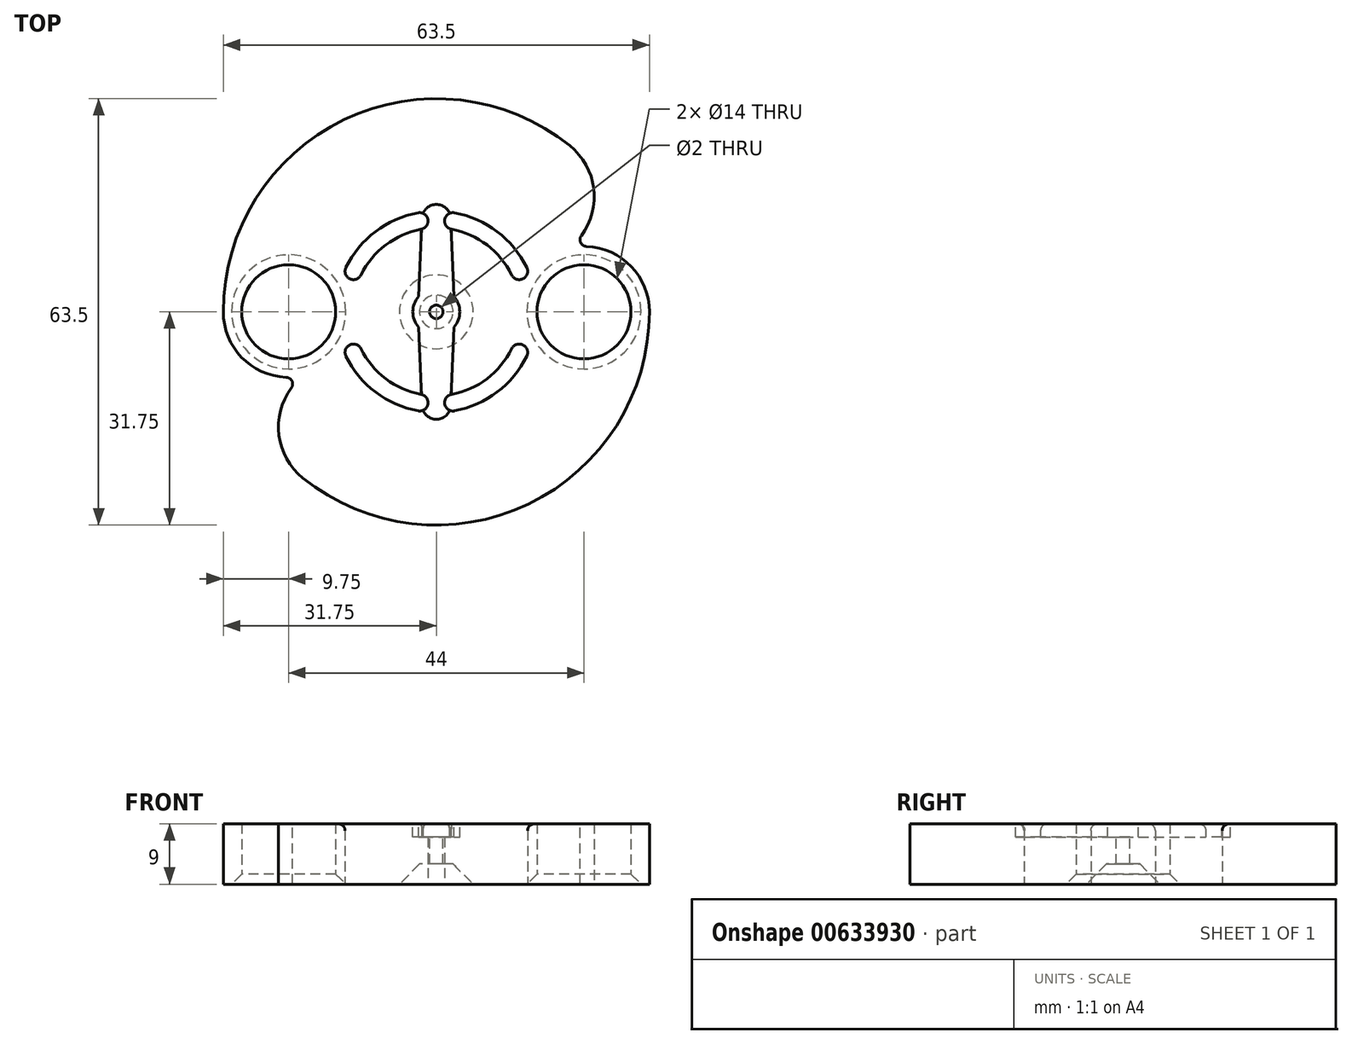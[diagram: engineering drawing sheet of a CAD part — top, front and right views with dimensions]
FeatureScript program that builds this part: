
annotation { "Feature Type Name" : "Feature", "Feature Type Description" : "" }
export const myFeature = defineFeature(function(context is Context, id is Id, definition is map)
    precondition{}
    {
        {
            var Q0;
            Q0=qCreatedBy(makeId("Top.planeOp"),FACE);
            var sketch = newSketch(context, id + "F0", { "sketchPlane" : qUnion([Q0])});
            skCircle(sketch, "E0", {"center": v(0, 0) * mm, "radius": 32.5 * mm});
            skCircle(sketch, "E1", {"center": v(0, 0) * mm, "radius": 2.5 * mm});
            skCircle(sketch, "E2", {"center": v(22, 0) * mm, "radius": 7 * mm});
            skLineSegment(sketch, "E3", {"start": v(0, 0) * mm, "end": v(22, 0) * mm, "construction": true});
            skLineSegment(sketch, "E4", {"start": v(0, 0) * mm, "end": v(-22, 0) * mm, "construction": true});
            skCircle(sketch, "E5", {"center": v(-22, 0) * mm, "radius": 7 * mm});
            skSolve(sketch);
        }
        {
            var Q0;
            Q0=qSketchRegion(id+"F0",true);
            extrude(context, id + "F1", {"entities" : qUnion([Q0]), "endBound" : BoundingType.SYMMETRIC, "depth" : 9 * mm, "offsetDistance" : 25 * mm});
        }
        {
            var Q0;
            Q0=makeQuery(id+"F1.opExtrude","CAP_FACE",FACE,{"disambiguationData":[OSD([sQuery(id+"F0.wireOp",EDGE,"E0"),sQuery(id+"F0.wireOp",EDGE,"E1"),sQuery(id+"F0.wireOp",EDGE,"E2")])],"isStart":false});
            var sketch = newSketch(context, id + "F2", { "sketchPlane" : qUnion([Q0])});
            skCircle(sketch, "E6", {"center": v(0, 0) * mm, "radius": 1 * mm});
            skCircle(sketch, "E7", {"center": v(0, 0) * mm, "radius": 2.5 * mm});
            skSolve(sketch);
        }
        {
            var Q0;
            Q0=qSketchRegion(id+"F2",true);
            extrude(context, id + "F3", {"entities" : qUnion([Q0]), "operationType" : NewBodyOperationType.ADD, "oppositeDirection" : true, "depth" : 6 * mm, "offsetDistance" : 25 * mm});
        }
        {
            var Q0;
            Q0=makeQuery(id+"F1.opExtrude","CAP_FACE",FACE,{"disambiguationData":[OSD([sQuery(id+"F0.wireOp",EDGE,"E0"),sQuery(id+"F0.wireOp",EDGE,"E1"),sQuery(id+"F0.wireOp",EDGE,"E2")])],"isStart":true});
            var sketch = newSketch(context, id + "F4", { "sketchPlane" : qUnion([Q0])});
            skLineSegment(sketch, "E8", {"start": v(0, 0) * mm, "end": v(22, 0) * mm, "construction": true});
            skCircle(sketch, "E9", {"center": v(0, 0) * mm, "radius": 32.5 * mm});
            skArc(sketch, "E10", {"start": v(12.25, 0) * mm, "mid": v(5.3, 11.05) * mm, "end": v(-7.67, 9.55) * mm});
            skArc(sketch, "E11", {"start": v(31.75, 0) * mm, "mid": v(13.72, 28.63) * mm, "end": v(-19.9, 24.75) * mm});
            skLineSegment(sketch, "E12", {"start": v(0, 0) * mm, "end": v(-22, 0) * mm, "construction": true});
            skArc(sketch, "E13", {"start": v(-12.25, 0) * mm, "mid": v(-22, 9.75) * mm, "end": v(-31.75, 0) * mm});
            skArc(sketch, "E14", {"start": v(12.25, 0) * mm, "mid": v(22, -9.75) * mm, "end": v(31.75, 0) * mm});
            skCircle(sketch, "E15", {"center": v(0, 0) * mm, "radius": 22 * mm, "construction": true});
            skArc(sketch, "E16", {"start": v(-15.94, 7.64) * mm, "mid": v(-11.6, 7.65) * mm, "end": v(-7.67, 9.55) * mm});
            skArc(sketch, "E17.trimOffspring", {"start": v(-19.9, 24.75) * mm, "mid": v(-23.53, 17.12) * mm, "end": v(-19.84, 9.5) * mm});
            skArc(sketch, "E18", {"start": v(15.94, -7.64) * mm, "mid": v(11.6, -7.65) * mm, "end": v(7.67, -9.55) * mm});
            skArc(sketch, "E19.trimOffspring", {"start": v(19.9, -24.75) * mm, "mid": v(23.53, -17.12) * mm, "end": v(19.84, -9.5) * mm});
            skArc(sketch, "E20.trimOffspring", {"start": v(-12.25, 0) * mm, "mid": v(-5.3, -11.05) * mm, "end": v(7.67, -9.55) * mm});
            skArc(sketch, "E21.trimOffspring", {"start": v(-31.75, 0) * mm, "mid": v(-13.72, -28.63) * mm, "end": v(19.9, -24.75) * mm});
            skSolve(sketch);
        }
        {
            var Q0;
            Q0=qSketchRegion(id+"F4",true);
            extrude(context, id + "F5", {"entities" : qUnion([Q0]), "operationType" : NewBodyOperationType.REMOVE, "oppositeDirection" : true, "depth" : 5 * mm, "offsetDistance" : 25 * mm});
        }
        {
            var Q0;
            Q0=makeQuery(id+"F3.boolean.opBoolean","MERGE",FACE,{"derivedFrom":[makeQuery(id+"F1.opExtrude","CAP_FACE",FACE,{"disambiguationData":[OSD([sQuery(id+"F0.wireOp",EDGE,"E0"),sQuery(id+"F0.wireOp",EDGE,"E1"),sQuery(id+"F0.wireOp",EDGE,"E2")])],"isStart":false}),makeQuery(id+"F3.opExtrude","CAP_FACE",FACE,{"disambiguationData":[OSD([sQuery(id+"F2.wireOp",EDGE,"E6"),sQuery(id+"F2.wireOp",EDGE,"E7")])],"isStart":true})]});
            var sketch = newSketch(context, id + "F6", { "sketchPlane" : qUnion([Q0])});
            skCircle(sketch, "E22", {"center": v(0, 0) * mm, "radius": 3.5 * mm});
            skLineSegment(sketch, "E23", {"start": v(0, 0) * mm, "end": v(0, 16) * mm, "construction": true});
            skLineSegment(sketch, "E24", {"start": v(0, 0) * mm, "end": v(0, -16) * mm, "construction": true});
            skArc(sketch, "E25", {"start": v(2.15, 13.85) * mm, "mid": v(0, 16) * mm, "end": v(-2.15, 13.85) * mm});
            skArc(sketch, "E26", {"start": v(-2.15, -13.85) * mm, "mid": v(0, -16) * mm, "end": v(2.15, -13.85) * mm});
            skLineSegment(sketch, "E27", {"start": v(-2.65, -2.29) * mm, "end": v(2.65, -2.29) * mm, "construction": true});
            skLineSegment(sketch, "E28", {"start": v(2.65, 2.29) * mm, "end": v(-2.65, 2.29) * mm, "construction": true});
            skLineSegment(sketch, "E29", {"start": v(2.65, -2.29) * mm, "end": v(2.15, -13.85) * mm});
            skLineSegment(sketch, "E30", {"start": v(-2.15, -13.85) * mm, "end": v(-2.65, -2.29) * mm});
            skLineSegment(sketch, "E31", {"start": v(-2.65, 2.29) * mm, "end": v(-2.15, 13.85) * mm});
            skLineSegment(sketch, "E32", {"start": v(2.65, 2.29) * mm, "end": v(2.15, 13.85) * mm});
            skSolve(sketch);
        }
        {
            var Q0;
            Q0=qSketchRegion(id+"F6",true);
            extrude(context, id + "F7", {"entities" : qUnion([Q0]), "operationType" : NewBodyOperationType.REMOVE, "oppositeDirection" : true, "depth" : 2 * mm, "offsetDistance" : 25 * mm});
        }
        {
            var Q0;
            Q0=qSketchRegion(id+"F6",true);
            extrude(context, id + "F8", {"entities" : qUnion([Q0]), "operationType" : NewBodyOperationType.REMOVE, "oppositeDirection" : true, "depth" : 2 * mm, "offsetDistance" : 25 * mm});
        }
        {
            var Q0;
            Q0=makeQuery(id+"F5.boolean.opBoolean","COPY",FACE,{"derivedFrom":makeQuery(id+"F5.opExtrude","CAP_FACE",FACE,{"disambiguationData":[OSD([sQuery(id+"F4.wireOp",EDGE,"E9"),sQuery(id+"F4.wireOp",EDGE,"E11"),sQuery(id+"F4.wireOp",EDGE,"E13"),sQuery(id+"F4.wireOp",EDGE,"E14"),sQuery(id+"F4.wireOp",EDGE,"E17.trimOffspring"),sQuery(id+"F4.wireOp",EDGE,"E19.trimOffspring"),sQuery(id+"F4.wireOp",EDGE,"E21.trimOffspring")])],"isStart":false})});
            var sketch = newSketch(context, id + "F9", { "sketchPlane" : qUnion([Q0])});
            skArc(sketch, "E33", {"start": v(19.84, -9.5) * mm, "mid": v(28.08, -7.62) * mm, "end": v(31.75, 0) * mm});
            skArc(sketch, "E34", {"start": v(-19.84, 9.5) * mm, "mid": v(-28.08, 7.62) * mm, "end": v(-31.75, 0) * mm});
            skArc(sketch, "E35", {"start": v(-19.9, 24.75) * mm, "mid": v(-23.53, 17.12) * mm, "end": v(-19.84, 9.5) * mm});
            skArc(sketch, "E36", {"start": v(31.75, 0) * mm, "mid": v(13.72, 28.63) * mm, "end": v(-19.9, 24.75) * mm});
            skCircle(sketch, "E37", {"center": v(0, 0) * mm, "radius": 32.5 * mm});
            skArc(sketch, "E38.trimOffspring", {"start": v(-31.75, 0) * mm, "mid": v(-13.72, -28.63) * mm, "end": v(19.9, -24.75) * mm});
            skArc(sketch, "E39", {"start": v(19.9, -24.75) * mm, "mid": v(23.53, -17.12) * mm, "end": v(19.84, -9.5) * mm});
            skSolve(sketch);
        }
        {
            var Q0;
            Q0=qSketchRegion(id+"F9",true);
            extrude(context, id + "F10", {"entities" : qUnion([Q0]), "operationType" : NewBodyOperationType.REMOVE, "endBound" : BoundingType.THROUGH_ALL, "oppositeDirection" : true, "depth" : 25 * mm, "offsetDistance" : 25 * mm});
        }
        {
            var Q0;
            Q0=makeQuery(id+"F1.opExtrude","CAP_FACE",FACE,{"disambiguationData":[OSD([sQuery(id+"F0.wireOp",EDGE,"E0"),sQuery(id+"F0.wireOp",EDGE,"E1"),sQuery(id+"F0.wireOp",EDGE,"E2"),sQuery(id+"F0.wireOp",EDGE,"E5")])],"isStart":true});
            var sketch = newSketch(context, id + "F11", { "sketchPlane" : qUnion([Q0])});
            skArc(sketch, "E40", {"start": v(2.71, -14.75) * mm, "mid": v(9.07, -11.95) * mm, "end": v(13.48, -6.59) * mm});
            skArc(sketch, "E41", {"start": v(2.26, -12.3) * mm, "mid": v(7.55, -9.96) * mm, "end": v(11.23, -5.49) * mm});
            skArc(sketch, "E42", {"start": v(11.23, 5.49) * mm, "mid": v(12.9, 4.92) * mm, "end": v(13.48, 6.59) * mm});
            skArc(sketch, "E43", {"start": v(13.48, -6.59) * mm, "mid": v(12.9, -4.92) * mm, "end": v(11.23, -5.49) * mm});
            skArc(sketch, "E44", {"start": v(-2.71, -14.75) * mm, "mid": v(-1.26, -13.75) * mm, "end": v(-2.26, -12.3) * mm});
            skArc(sketch, "E45", {"start": v(2.26, -12.3) * mm, "mid": v(1.26, -13.75) * mm, "end": v(2.71, -14.75) * mm});
            skArc(sketch, "E46", {"start": v(-2.26, 12.3) * mm, "mid": v(-1.26, 13.75) * mm, "end": v(-2.71, 14.75) * mm});
            skArc(sketch, "E47", {"start": v(2.71, 14.75) * mm, "mid": v(1.26, 13.75) * mm, "end": v(2.26, 12.3) * mm});
            skArc(sketch, "E48.trimOffspring", {"start": v(11.23, 5.49) * mm, "mid": v(7.55, 9.96) * mm, "end": v(2.26, 12.3) * mm});
            skArc(sketch, "E49.trimOffspring", {"start": v(13.48, 6.59) * mm, "mid": v(9.07, 11.95) * mm, "end": v(2.71, 14.75) * mm});
            skArc(sketch, "E50.trimOffspring", {"start": v(-2.26, 12.3) * mm, "mid": v(-7.55, 9.96) * mm, "end": v(-11.23, 5.5) * mm});
            skArc(sketch, "E51.trimOffspring", {"start": v(-2.71, 14.75) * mm, "mid": v(-9.06, 11.95) * mm, "end": v(-13.47, 6.6) * mm});
            skArc(sketch, "E52.trimOffspring", {"start": v(-13.48, -6.59) * mm, "mid": v(-9.07, -11.95) * mm, "end": v(-2.71, -14.75) * mm});
            skArc(sketch, "E53.trimOffspring", {"start": v(-11.23, -5.49) * mm, "mid": v(-7.55, -9.96) * mm, "end": v(-2.26, -12.3) * mm});
            skArc(sketch, "E54", {"start": v(-11.23, -5.49) * mm, "mid": v(-12.9, -4.92) * mm, "end": v(-13.48, -6.59) * mm});
            skArc(sketch, "E55", {"start": v(-13.47, 6.6) * mm, "mid": v(-12.9, 4.92) * mm, "end": v(-11.23, 5.5) * mm});
            skSolve(sketch);
        }
        {
            var Q0;
            Q0=qSketchRegion(id+"F11",true);
            extrude(context, id + "F12", {"entities" : qUnion([Q0]), "operationType" : NewBodyOperationType.REMOVE, "endBound" : BoundingType.THROUGH_ALL, "oppositeDirection" : true, "depth" : 25 * mm, "offsetDistance" : 25 * mm});
        }
        {
            var Q0;
            Q0=makeQuery(id+"F1.opExtrude","CAP_EDGE",EDGE,{"disambiguationData":[OSD([sQuery(id+"F0.wireOp",EDGE,"E2")])],"isStart":true});
            var Q1;
            Q1=makeQuery(id+"F1.opExtrude","CAP_EDGE",EDGE,{"disambiguationData":[OSD([sQuery(id+"F0.wireOp",EDGE,"E5")])],"isStart":true});
            chamfer(context, id + "F13", {"entities" : qUnion([Q0, Q1]), "width" : 1.5 * mm, "tangentPropagation" : true});
        }
        {
            var Q0;
            Q0=makeQuery(id+"F10.boolean.opBoolean","MERGE",EDGE,{"derivedFrom":[makeQuery(id+"F5.boolean.opBoolean","COPY",EDGE,{"derivedFrom":makeQuery(id+"F5.opExtrude","SWEPT_EDGE",EDGE,{"disambiguationData":[OSD([sQuery(id+"F4.wireOp",EDGE,"E13"),sQuery(id+"F4.wireOp",EDGE,"E17.trimOffspring")])]})}),makeQuery(id+"F10.opExtrude","SWEPT_EDGE",EDGE,{"disambiguationData":[OSD([sQuery(id+"F9.wireOp",EDGE,"E34"),sQuery(id+"F9.wireOp",EDGE,"E35")])]})]});
            var Q1;
            Q1=makeQuery(id+"F10.boolean.opBoolean","MERGE",EDGE,{"derivedFrom":[makeQuery(id+"F5.boolean.opBoolean","COPY",EDGE,{"derivedFrom":makeQuery(id+"F5.opExtrude","SWEPT_EDGE",EDGE,{"disambiguationData":[OSD([sQuery(id+"F4.wireOp",EDGE,"E14"),sQuery(id+"F4.wireOp",EDGE,"E19.trimOffspring")])]})}),makeQuery(id+"F10.opExtrude","SWEPT_EDGE",EDGE,{"disambiguationData":[OSD([sQuery(id+"F9.wireOp",EDGE,"E33"),sQuery(id+"F9.wireOp",EDGE,"E39")])]})]});
            fillet(context, id + "F14", {"entities" : qUnion([Q0, Q1]), "radius" : 1 * mm, "tangentPropagation" : true, "allowEdgeOverflow" : false});
        }
        {
            var Q0;
            Q0=makeQuery(id+"F12.boolean.opBoolean","INTERSECT",EDGE,{"derivedFrom":[makeQuery(id+"F3.boolean.opBoolean","MERGE",FACE,{"derivedFrom":[makeQuery(id+"F1.opExtrude","CAP_FACE",FACE,{"disambiguationData":[OSD([sQuery(id+"F0.wireOp",EDGE,"E0"),sQuery(id+"F0.wireOp",EDGE,"E1"),sQuery(id+"F0.wireOp",EDGE,"E2"),sQuery(id+"F0.wireOp",EDGE,"E5")])],"isStart":false}),makeQuery(id+"F3.opExtrude","CAP_FACE",FACE,{"disambiguationData":[OSD([sQuery(id+"F2.wireOp",EDGE,"E6"),sQuery(id+"F2.wireOp",EDGE,"E7")])],"isStart":true})]}),makeQuery(id+"F12.opExtrude","SWEPT_FACE",FACE,{"disambiguationData":[OSD([sQuery(id+"F11.wireOp",EDGE,"E52.trimOffspring")])]})]});
            var Q1;
            Q1=makeQuery(id+"F12.boolean.opBoolean","INTERSECT",EDGE,{"derivedFrom":[makeQuery(id+"F3.boolean.opBoolean","MERGE",FACE,{"derivedFrom":[makeQuery(id+"F1.opExtrude","CAP_FACE",FACE,{"disambiguationData":[OSD([sQuery(id+"F0.wireOp",EDGE,"E0"),sQuery(id+"F0.wireOp",EDGE,"E1"),sQuery(id+"F0.wireOp",EDGE,"E2"),sQuery(id+"F0.wireOp",EDGE,"E5")])],"isStart":false}),makeQuery(id+"F3.opExtrude","CAP_FACE",FACE,{"disambiguationData":[OSD([sQuery(id+"F2.wireOp",EDGE,"E6"),sQuery(id+"F2.wireOp",EDGE,"E7")])],"isStart":true})]}),makeQuery(id+"F12.opExtrude","SWEPT_FACE",FACE,{"disambiguationData":[OSD([sQuery(id+"F11.wireOp",EDGE,"E51.trimOffspring")])]})]});
            var Q2;
            Q2=makeQuery(id+"F12.boolean.opBoolean","COPY",EDGE,{"derivedFrom":makeQuery(id+"F12.opExtrude","CAP_EDGE",EDGE,{"disambiguationData":[OSD([sQuery(id+"F11.wireOp",EDGE,"E51.trimOffspring")])],"isStart":true})});
            var Q3;
            Q3=makeQuery(id+"F12.boolean.opBoolean","INTERSECT",EDGE,{"derivedFrom":[makeQuery(id+"F3.boolean.opBoolean","MERGE",FACE,{"derivedFrom":[makeQuery(id+"F1.opExtrude","CAP_FACE",FACE,{"disambiguationData":[OSD([sQuery(id+"F0.wireOp",EDGE,"E0"),sQuery(id+"F0.wireOp",EDGE,"E1"),sQuery(id+"F0.wireOp",EDGE,"E2"),sQuery(id+"F0.wireOp",EDGE,"E5")])],"isStart":false}),makeQuery(id+"F3.opExtrude","CAP_FACE",FACE,{"disambiguationData":[OSD([sQuery(id+"F2.wireOp",EDGE,"E6"),sQuery(id+"F2.wireOp",EDGE,"E7")])],"isStart":true})]}),makeQuery(id+"F12.opExtrude","SWEPT_FACE",FACE,{"disambiguationData":[OSD([sQuery(id+"F11.wireOp",EDGE,"E49.trimOffspring")])]})]});
            var Q4;
            Q4=makeQuery(id+"F12.boolean.opBoolean","COPY",EDGE,{"derivedFrom":makeQuery(id+"F12.opExtrude","CAP_EDGE",EDGE,{"disambiguationData":[OSD([sQuery(id+"F11.wireOp",EDGE,"E49.trimOffspring")])],"isStart":true})});
            var Q5;
            Q5=makeQuery(id+"F12.boolean.opBoolean","COPY",EDGE,{"derivedFrom":makeQuery(id+"F12.opExtrude","CAP_EDGE",EDGE,{"disambiguationData":[OSD([sQuery(id+"F11.wireOp",EDGE,"E40")])],"isStart":true})});
            var Q6;
            Q6=makeQuery(id+"F12.boolean.opBoolean","INTERSECT",EDGE,{"derivedFrom":[makeQuery(id+"F3.boolean.opBoolean","MERGE",FACE,{"derivedFrom":[makeQuery(id+"F1.opExtrude","CAP_FACE",FACE,{"disambiguationData":[OSD([sQuery(id+"F0.wireOp",EDGE,"E0"),sQuery(id+"F0.wireOp",EDGE,"E1"),sQuery(id+"F0.wireOp",EDGE,"E2"),sQuery(id+"F0.wireOp",EDGE,"E5")])],"isStart":false}),makeQuery(id+"F3.opExtrude","CAP_FACE",FACE,{"disambiguationData":[OSD([sQuery(id+"F2.wireOp",EDGE,"E6"),sQuery(id+"F2.wireOp",EDGE,"E7")])],"isStart":true})]}),makeQuery(id+"F12.opExtrude","SWEPT_FACE",FACE,{"disambiguationData":[OSD([sQuery(id+"F11.wireOp",EDGE,"E40")])]})]});
            var Q7;
            Q7=makeQuery(id+"F12.boolean.opBoolean","COPY",EDGE,{"derivedFrom":makeQuery(id+"F12.opExtrude","CAP_EDGE",EDGE,{"disambiguationData":[OSD([sQuery(id+"F11.wireOp",EDGE,"E52.trimOffspring")])],"isStart":true})});
            var Q8;
            Q8=makeQuery(id+"F12.boolean.opBoolean","INTERSECT",EDGE,{"derivedFrom":[makeQuery(id+"F3.boolean.opBoolean","MERGE",FACE,{"derivedFrom":[makeQuery(id+"F1.opExtrude","CAP_FACE",FACE,{"disambiguationData":[OSD([sQuery(id+"F0.wireOp",EDGE,"E0"),sQuery(id+"F0.wireOp",EDGE,"E1"),sQuery(id+"F0.wireOp",EDGE,"E2"),sQuery(id+"F0.wireOp",EDGE,"E5")])],"isStart":false}),makeQuery(id+"F3.opExtrude","CAP_FACE",FACE,{"disambiguationData":[OSD([sQuery(id+"F2.wireOp",EDGE,"E6"),sQuery(id+"F2.wireOp",EDGE,"E7")])],"isStart":true})]}),makeQuery(id+"F12.opExtrude","SWEPT_FACE",FACE,{"disambiguationData":[OSD([sQuery(id+"F11.wireOp",EDGE,"E47")])]})]});
            var Q9;
            Q9=makeQuery(id+"F12.boolean.opBoolean","INTERSECT",EDGE,{"derivedFrom":[makeQuery(id+"F3.boolean.opBoolean","MERGE",FACE,{"derivedFrom":[makeQuery(id+"F1.opExtrude","CAP_FACE",FACE,{"disambiguationData":[OSD([sQuery(id+"F0.wireOp",EDGE,"E0"),sQuery(id+"F0.wireOp",EDGE,"E1"),sQuery(id+"F0.wireOp",EDGE,"E2"),sQuery(id+"F0.wireOp",EDGE,"E5")])],"isStart":false}),makeQuery(id+"F3.opExtrude","CAP_FACE",FACE,{"disambiguationData":[OSD([sQuery(id+"F2.wireOp",EDGE,"E6"),sQuery(id+"F2.wireOp",EDGE,"E7")])],"isStart":true})]}),makeQuery(id+"F12.opExtrude","SWEPT_FACE",FACE,{"disambiguationData":[OSD([sQuery(id+"F11.wireOp",EDGE,"E46")])]})]});
            var Q10;
            Q10=makeQuery(id+"F12.boolean.opBoolean","INTERSECT",EDGE,{"derivedFrom":[makeQuery(id+"F3.boolean.opBoolean","MERGE",FACE,{"derivedFrom":[makeQuery(id+"F1.opExtrude","CAP_FACE",FACE,{"disambiguationData":[OSD([sQuery(id+"F0.wireOp",EDGE,"E0"),sQuery(id+"F0.wireOp",EDGE,"E1"),sQuery(id+"F0.wireOp",EDGE,"E2"),sQuery(id+"F0.wireOp",EDGE,"E5")])],"isStart":false}),makeQuery(id+"F3.opExtrude","CAP_FACE",FACE,{"disambiguationData":[OSD([sQuery(id+"F2.wireOp",EDGE,"E6"),sQuery(id+"F2.wireOp",EDGE,"E7")])],"isStart":true})]}),makeQuery(id+"F12.opExtrude","SWEPT_FACE",FACE,{"disambiguationData":[OSD([sQuery(id+"F11.wireOp",EDGE,"IULc2HyE-kvyv-PGGa-Ogag-i5b3ODiteL6P")])]})]});
            var Q11;
            Q11=makeQuery(id+"F12.boolean.opBoolean","INTERSECT",EDGE,{"derivedFrom":[makeQuery(id+"F3.boolean.opBoolean","MERGE",FACE,{"derivedFrom":[makeQuery(id+"F1.opExtrude","CAP_FACE",FACE,{"disambiguationData":[OSD([sQuery(id+"F0.wireOp",EDGE,"E0"),sQuery(id+"F0.wireOp",EDGE,"E1"),sQuery(id+"F0.wireOp",EDGE,"E2"),sQuery(id+"F0.wireOp",EDGE,"E5")])],"isStart":false}),makeQuery(id+"F3.opExtrude","CAP_FACE",FACE,{"disambiguationData":[OSD([sQuery(id+"F2.wireOp",EDGE,"E6"),sQuery(id+"F2.wireOp",EDGE,"E7")])],"isStart":true})]}),makeQuery(id+"F12.opExtrude","SWEPT_FACE",FACE,{"disambiguationData":[OSD([sQuery(id+"F11.wireOp",EDGE,"LXNWlSoz-vkBC-R6Zu-CKnh-kSYyZzRBl4sp")])]})]});
            var Q12;
            Q12=makeQuery(id+"F12.boolean.opBoolean","INTERSECT",EDGE,{"derivedFrom":[makeQuery(id+"F3.boolean.opBoolean","MERGE",FACE,{"derivedFrom":[makeQuery(id+"F1.opExtrude","CAP_FACE",FACE,{"disambiguationData":[OSD([sQuery(id+"F0.wireOp",EDGE,"E0"),sQuery(id+"F0.wireOp",EDGE,"E1"),sQuery(id+"F0.wireOp",EDGE,"E2"),sQuery(id+"F0.wireOp",EDGE,"E5")])],"isStart":false}),makeQuery(id+"F3.opExtrude","CAP_FACE",FACE,{"disambiguationData":[OSD([sQuery(id+"F2.wireOp",EDGE,"E6"),sQuery(id+"F2.wireOp",EDGE,"E7")])],"isStart":true})]}),makeQuery(id+"F12.opExtrude","SWEPT_FACE",FACE,{"disambiguationData":[OSD([sQuery(id+"F11.wireOp",EDGE,"E42")])]})]});
            var Q13;
            Q13=makeQuery(id+"F12.boolean.opBoolean","INTERSECT",EDGE,{"derivedFrom":[makeQuery(id+"F3.boolean.opBoolean","MERGE",FACE,{"derivedFrom":[makeQuery(id+"F1.opExtrude","CAP_FACE",FACE,{"disambiguationData":[OSD([sQuery(id+"F0.wireOp",EDGE,"E0"),sQuery(id+"F0.wireOp",EDGE,"E1"),sQuery(id+"F0.wireOp",EDGE,"E2"),sQuery(id+"F0.wireOp",EDGE,"E5")])],"isStart":false}),makeQuery(id+"F3.opExtrude","CAP_FACE",FACE,{"disambiguationData":[OSD([sQuery(id+"F2.wireOp",EDGE,"E6"),sQuery(id+"F2.wireOp",EDGE,"E7")])],"isStart":true})]}),makeQuery(id+"F12.opExtrude","SWEPT_FACE",FACE,{"disambiguationData":[OSD([sQuery(id+"F11.wireOp",EDGE,"E43")])]})]});
            var Q14;
            Q14=makeQuery(id+"F12.boolean.opBoolean","INTERSECT",EDGE,{"derivedFrom":[makeQuery(id+"F3.boolean.opBoolean","MERGE",FACE,{"derivedFrom":[makeQuery(id+"F1.opExtrude","CAP_FACE",FACE,{"disambiguationData":[OSD([sQuery(id+"F0.wireOp",EDGE,"E0"),sQuery(id+"F0.wireOp",EDGE,"E1"),sQuery(id+"F0.wireOp",EDGE,"E2"),sQuery(id+"F0.wireOp",EDGE,"E5")])],"isStart":false}),makeQuery(id+"F3.opExtrude","CAP_FACE",FACE,{"disambiguationData":[OSD([sQuery(id+"F2.wireOp",EDGE,"E6"),sQuery(id+"F2.wireOp",EDGE,"E7")])],"isStart":true})]}),makeQuery(id+"F12.opExtrude","SWEPT_FACE",FACE,{"disambiguationData":[OSD([sQuery(id+"F11.wireOp",EDGE,"E45")])]})]});
            fillet(context, id + "F15", {"entities" : qUnion([Q0, Q1, Q2, Q3, Q4, Q5, Q6, Q7, Q8, Q9, Q10, Q11, Q12, Q13, Q14]), "radius" : 1 * mm, "tangentPropagation" : true, "allowEdgeOverflow" : false});
        }
        {
            var Q0;
            Q0=makeQuery(id+"F1.opExtrude","CAP_EDGE",EDGE,{"disambiguationData":[OSD([sQuery(id+"F0.wireOp",EDGE,"E1")])],"isStart":true});
            chamfer(context, id + "F16", {"entities" : qUnion([Q0]), "chamferType" : ChamferType.OFFSET_ANGLE, "width" : 3 * mm, "oppositeDirection" : false, "angle" : 45 * degree, "tangentPropagation" : true});
        }
    });
